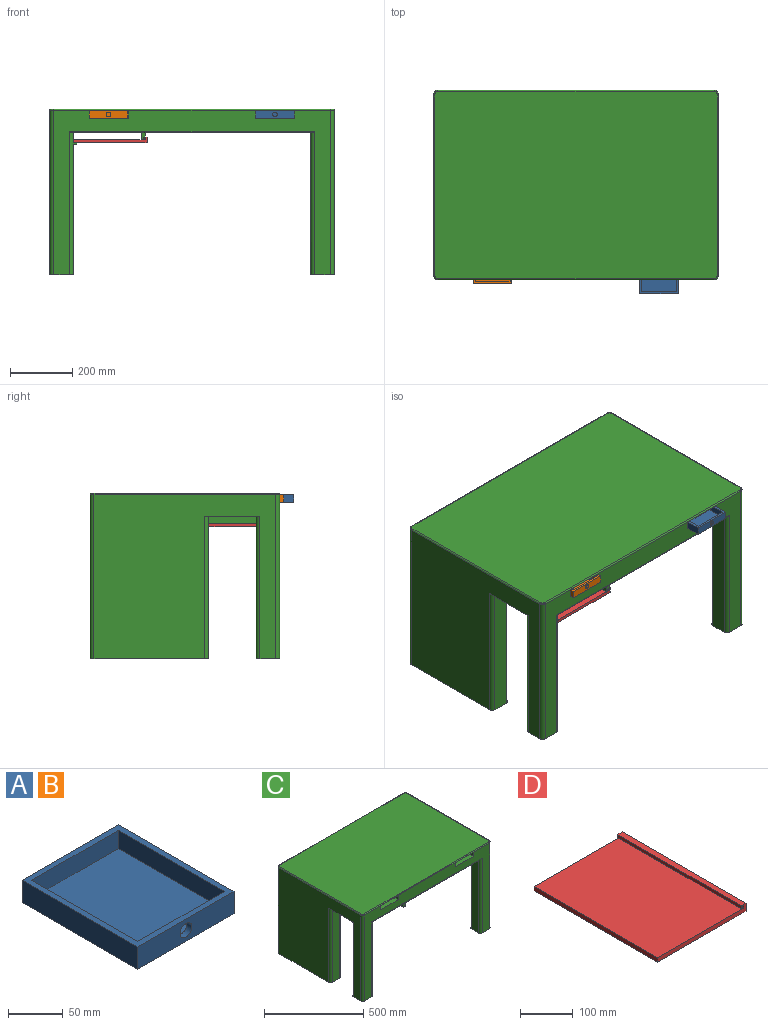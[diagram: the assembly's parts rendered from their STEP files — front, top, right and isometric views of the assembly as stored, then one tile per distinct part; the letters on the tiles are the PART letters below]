
ASSEMBLY  parts=4 mates=3
PART A: 12 faces, bbox 124.5x149.9x24.9 mm
  f0: plane 149.86x124.46mm, normal (0,0,1), area 3322.6mm2, adj f1,f2,f3,f4,f7,f8,f9,f10
  f1: plane 124.46x24.89mm, normal (0,-1,0), area 2915.6mm2, adj f0,f2,f4,f5,f6
  f2: plane 149.86x24.89mm, normal (1,0,0), area 3730.3mm2, adj f0,f1,f3,f5
  f3: plane 124.46x24.89mm, normal (0,1,0), area 3098.1mm2, adj f0,f2,f4,f5
  f4: plane 149.86x24.89mm, normal (-1,0,0), area 3730.3mm2, adj f0,f1,f3,f5
  f5: plane 149.86x124.46mm, normal (0,0,-1), area 18651.6mm2, adj f1,f2,f3,f4
  f6: cylinder r=7.62mm len=15.24mm, axis (0,-1,0), area 304mm2, adj f1,f7
  f7: plane 111.76x20.32mm, normal (0,1,0), area 2088.5mm2, adj f0,f6,f8,f10,f11
  f8: plane 137.16x20.32mm, normal (-1,0,0), area 2787.1mm2, adj f0,f7,f9,f11
  f9: plane 111.76x20.32mm, normal (0,-1,0), area 2271mm2, adj f0,f8,f10,f11
  f10: plane 137.16x20.32mm, normal (1,0,0), area 2787.1mm2, adj f0,f7,f9,f11
  f11: plane 137.16x111.76mm, normal (0,0,1), area 15329mm2, adj f7,f8,f9,f10
PART B: same geometry as A
PART C: 75 faces, bbox 916.5x611.7x533.4 mm
  f0: plane 418.47x50.8mm, normal (1,0,0), area 21258mm2, adj f11,f40,f41,f65
  f1: plane 330.2x13.84mm, normal (1,0,0), area 4571.2mm2, adj f2,f3,f56,f60
  f2: plane 22.86x11.43mm, normal (0,1,0), area 228.2mm2, adj f1,f3,f57,f58,f59,f60,f61,f62
  f3: plane 914.4x605.79mm, normal (0,0,-1), area 504655.6mm2, adj f1,f2,f5,f6,f7,f9,f10,f12
  f4: plane 889x529.59mm, normal (0,-1,0), area 101420.8mm2, adj f11,f17,f21,f22,f23,f24,f26,f27
  f5: plane 584.2x529.59mm, normal (1,0,0), area 88741.8mm2, adj f3,f17,f20,f33,f36,f43,f44,f50
  f6: plane 889x529.59mm, normal (0,1,0), area 110806.2mm2, adj f3,f14,f20,f31,f38,f44,f45,f47
  f7: plane 584.2x529.59mm, normal (-1,0,0), area 228096.3mm2, adj f3,f11,f14,f37,f42,f45,f46,f51
  f8: plane 906.78x601.98mm, normal (0,0,1), area 545795.6mm2, adj f47,f48,f49,f50,f51,f52,f53,f54
  f9: plane 457.2x50.8mm, normal (0,1,0), area 23225.8mm2, adj f3,f11,f41,f42
  f10: plane 50.8x32.39mm, normal (1,0,0), area 1645.2mm2, adj f3,f40,f41,f67
  f11: plane 76.2x76.2mm, normal (0,0,-1), area 5668mm2, adj f0,f4,f7,f9,f40,f41,f42,f46
  f12: plane 457.2x50.8mm, normal (0,-1,0), area 23225.8mm2, adj f3,f14,f37,f39
  f13: plane 457.2x355.6mm, normal (1,0,0), area 162236.8mm2, adj f3,f14,f38,f39,f71,f72,f73
  f14: plane 381x76.2mm, normal (0,0,-1), area 28893.7mm2, adj f6,f7,f12,f13,f37,f38,f39,f45
  f15: plane 457.2x50.8mm, normal (0,1,0), area 23225.8mm2, adj f3,f17,f34,f36
  f16: plane 457.2x50.8mm, normal (-1,0,0), area 23225.8mm2, adj f3,f17,f34,f35
  f17: plane 76.2x76.2mm, normal (0,0,-1), area 5668mm2, adj f4,f5,f15,f16,f34,f35,f36,f43
  f18: plane 457.2x50.8mm, normal (0,-1,0), area 23225.8mm2, adj f3,f20,f32,f33
  f19: plane 457.2x50.8mm, normal (-1,0,0), area 23225.8mm2, adj f3,f20,f31,f32
  f20: plane 76.2x76.2mm, normal (0,0,-1), area 5668mm2, adj f5,f6,f18,f19,f31,f32,f33,f44
  f21: plane 152.4x25.14mm, normal (-1,0,0), area 3831.3mm2, adj f4,f22,f24,f25
  f22: plane 152.4x127mm, normal (0,0,-1), area 19354.8mm2, adj f4,f21,f23,f25
  f23: plane 152.4x25.14mm, normal (1,0,0), area 3831.3mm2, adj f4,f22,f24,f25
  f24: plane 152.4x127mm, normal (0,0,1), area 19354.8mm2, adj f4,f21,f23,f25
  f25: plane 127x25.14mm, normal (0,-1,0), area 3192.7mm2, adj f21,f22,f23,f24
  f26: plane 152.4x127mm, normal (0,0,-1), area 19354.8mm2, adj f4,f27,f29,f30
  f27: plane 152.4x25.14mm, normal (1,0,0), area 3831.3mm2, adj f4,f26,f28,f30
  f28: plane 152.4x127mm, normal (0,0,1), area 19354.8mm2, adj f4,f27,f29,f30
  f29: plane 152.4x25.14mm, normal (-1,0,0), area 3831.3mm2, adj f4,f26,f28,f30
  f30: plane 127x25.14mm, normal (0,-1,0), area 3192.7mm2, adj f26,f27,f28,f29
  f31: cylinder r=12.7mm len=457.2mm, axis (0,0,-1), area 9120.7mm2, adj f3,f6,f19,f20
  f32: cylinder r=12.7mm len=457.2mm, axis (0,0,-1), area 9120.7mm2, adj f3,f18,f19,f20
  f33: cylinder r=12.7mm len=457.2mm, axis (0,0,1), area 9120.7mm2, adj f3,f5,f18,f20
  f34: cylinder r=12.7mm len=457.2mm, axis (0,0,-1), area 9120.7mm2, adj f3,f15,f16,f17
  f35: cylinder r=12.7mm len=461.01mm, axis (0,0,-1), area 9135.5mm2, adj f3,f4,f16,f17,f55
  f36: cylinder r=12.7mm len=457.2mm, axis (0,0,-1), area 9120.7mm2, adj f3,f5,f15,f17
  f37: cylinder r=12.7mm len=457.2mm, axis (0,0,1), area 9120.7mm2, adj f3,f7,f12,f14
  f38: cylinder r=12.7mm len=457.2mm, axis (0,0,1), area 9120.7mm2, adj f3,f6,f13,f14
  f39: cylinder r=12.7mm len=457.2mm, axis (0,0,-1), area 9120.7mm2, adj f3,f12,f13,f14,f70
  f40: cylinder r=12.7mm len=461.01mm, axis (0,0,1), area 9135.5mm2, adj f0,f3,f4,f10,f11,f55,f68
  f41: cylinder r=12.7mm len=457.2mm, axis (0,0,-1), area 9120.7mm2, adj f0,f3,f9,f10,f11,f66
  f42: cylinder r=12.7mm len=457.2mm, axis (0,0,-1), area 9120.7mm2, adj f3,f7,f9,f11
  f43: cylinder r=12.7mm len=529.59mm, axis (0,0,1), area 10564.9mm2, adj f4,f5,f17,f52
  f44: cylinder r=12.7mm len=529.59mm, axis (0,0,-1), area 10564.9mm2, adj f5,f6,f20,f48
  f45: cylinder r=12.7mm len=529.59mm, axis (0,0,1), area 10564.9mm2, adj f6,f7,f14,f49
  f46: cylinder r=12.7mm len=529.59mm, axis (0,0,-1), area 10564.9mm2, adj f4,f7,f11,f53
  f47: cylinder r=3.81mm len=889mm, axis (1,0,0), area 5320.4mm2, adj f6,f8,f48,f49
  f48: torus R=8.89mm, axis (0,0,1), area 106.4mm2, adj f8,f44,f47,f50
  f49: torus R=8.89mm, axis (0,0,1), area 106.4mm2, adj f8,f45,f47,f51
  f50: cylinder r=3.81mm len=584.2mm, axis (0,-1,0), area 3496.3mm2, adj f5,f8,f48,f52
  f51: cylinder r=3.81mm len=584.2mm, axis (0,1,0), area 3496.3mm2, adj f7,f8,f49,f53
  f52: torus R=8.89mm, axis (0,0,1), area 106.4mm2, adj f8,f43,f50,f54
  f53: torus R=8.89mm, axis (0,0,1), area 106.4mm2, adj f8,f46,f51,f54
  f54: cylinder r=3.81mm len=889mm, axis (-1,0,0), area 5320.4mm2, adj f4,f8,f52,f53
  f55: cylinder r=3.81mm len=787.4mm, axis (1,0,0), area 4652.8mm2, adj f3,f4,f35,f40,f56
  f56: plane 22.86x11.43mm, normal (0,-1,0), area 228.2mm2, adj f1,f55,f57,f58,f59,f60,f61,f62
  f57: plane 330.2x22.86mm, normal (-1,0,0), area 7548.4mm2, adj f2,f3,f56,f59
  f58: plane 330.2x5.72mm, normal (1,0,0), area 1887.1mm2, adj f2,f56,f59,f64
  f59: plane 330.2x11.43mm, normal (0,0,-1), area 3774.2mm2, adj f2,f56,f57,f58
  f60: plane 330.2x6.35mm, normal (0,0,-1), area 2096.8mm2, adj f1,f2,f56,f61
  f61: plane 330.2x7.11mm, normal (1,0,0), area 2348.1mm2, adj f2,f56,f60,f62
  f62: plane 330.2x3.18mm, normal (0,0,1), area 1048.4mm2, adj f2,f56,f61,f63
  f63: plane 330.2x3.81mm, normal (-1,0,0), area 1258.1mm2, adj f2,f56,f62,f64
  f64: plane 330.2x3.18mm, normal (0,0,1), area 1048.4mm2, adj f2,f56,f58,f63
  f65: plane 50.8x10.16mm, normal (0,0,-1), area 516.1mm2, adj f0,f66,f68,f69
  f66: plane 10.16x6.35mm, normal (0,1,0), area 64.5mm2, adj f41,f65,f67,f69
  f67: plane 50.8x10.16mm, normal (0,0,1), area 516.1mm2, adj f10,f66,f68,f69
  f68: plane 10.16x6.35mm, normal (0,-1,0), area 64.5mm2, adj f40,f65,f67,f69
  f69: plane 50.8x6.35mm, normal (1,0,0), area 322.6mm2, adj f65,f66,f67,f68
  f70: plane 10.16x5.59mm, normal (0,-1,0), area 56.8mm2, adj f39,f71,f73,f74
  f71: plane 61.47x10.16mm, normal (0,0,-1), area 624.5mm2, adj f13,f70,f72,f74
  f72: plane 10.16x5.59mm, normal (0,1,0), area 56.8mm2, adj f13,f71,f73,f74
  f73: plane 61.47x10.16mm, normal (0,0,1), area 624.5mm2, adj f13,f70,f72,f74
  f74: plane 61.47x5.59mm, normal (1,0,0), area 343.5mm2, adj f70,f71,f72,f73
PART D: 12 faces, bbox 236.2x330.2x18.7 mm
  f0: plane 330.2x3.18mm, normal (0,0,-1), area 1048.4mm2, adj f1,f2,f4,f10
  f1: plane 330.2x5.21mm, normal (-1,0,0), area 1719.4mm2, adj f0,f2,f4,f5
  f2: plane 236.22x18.67mm, normal (0,-1,0), area 2487.1mm2, adj f0,f1,f3,f5,f6,f7,f8,f9
  f3: plane 330.2x18.67mm, normal (1,0,0), area 6164.5mm2, adj f2,f4,f6,f7
  f4: plane 236.22x18.67mm, normal (0,1,0), area 2487.1mm2, adj f0,f1,f3,f5,f6,f7,f8,f9
  f5: plane 330.2x229.87mm, normal (0,0,1), area 75903.1mm2, adj f1,f2,f4,f11
  f6: plane 330.2x236.22mm, normal (0,0,-1), area 77999.8mm2, adj f2,f3,f4,f11
  f7: plane 330.2x12.7mm, normal (0,0,1), area 4193.5mm2, adj f2,f3,f4,f8
  f8: plane 330.2x7.11mm, normal (-1,0,0), area 2348.4mm2, adj f2,f4,f7,f9
  f9: plane 330.2x3.18mm, normal (0,0,-1), area 1048.4mm2, adj f2,f4,f8,f10
  f10: plane 330.2x3.81mm, normal (1,0,0), area 1258.1mm2, adj f0,f2,f4,f9
  f11: plane 330.2x10.16mm, normal (-1,0,0), area 3354.8mm2, adj f2,f4,f5,f6
PLACE A t=(266.7,-275.62,46.1)mm
PLACE B t=(-267.97,-242.29,45.98)mm
PLACE C at identity fixed
PLACE D t=(-258.9,-135.66,-32.51)mm
MATE slider C.f30 <-> B.f3  axis (0,-1,0) through (-330.2,-152.4,45.98)mm
MATE slider C.f25 <-> A.f3  axis (0,-1,0) through (266.7,-152.4,58.55)mm
MATE slider D.f2 <-> C.f56  axis (0,-1,0) through (-154.13,-300.76,-20.96)mm
